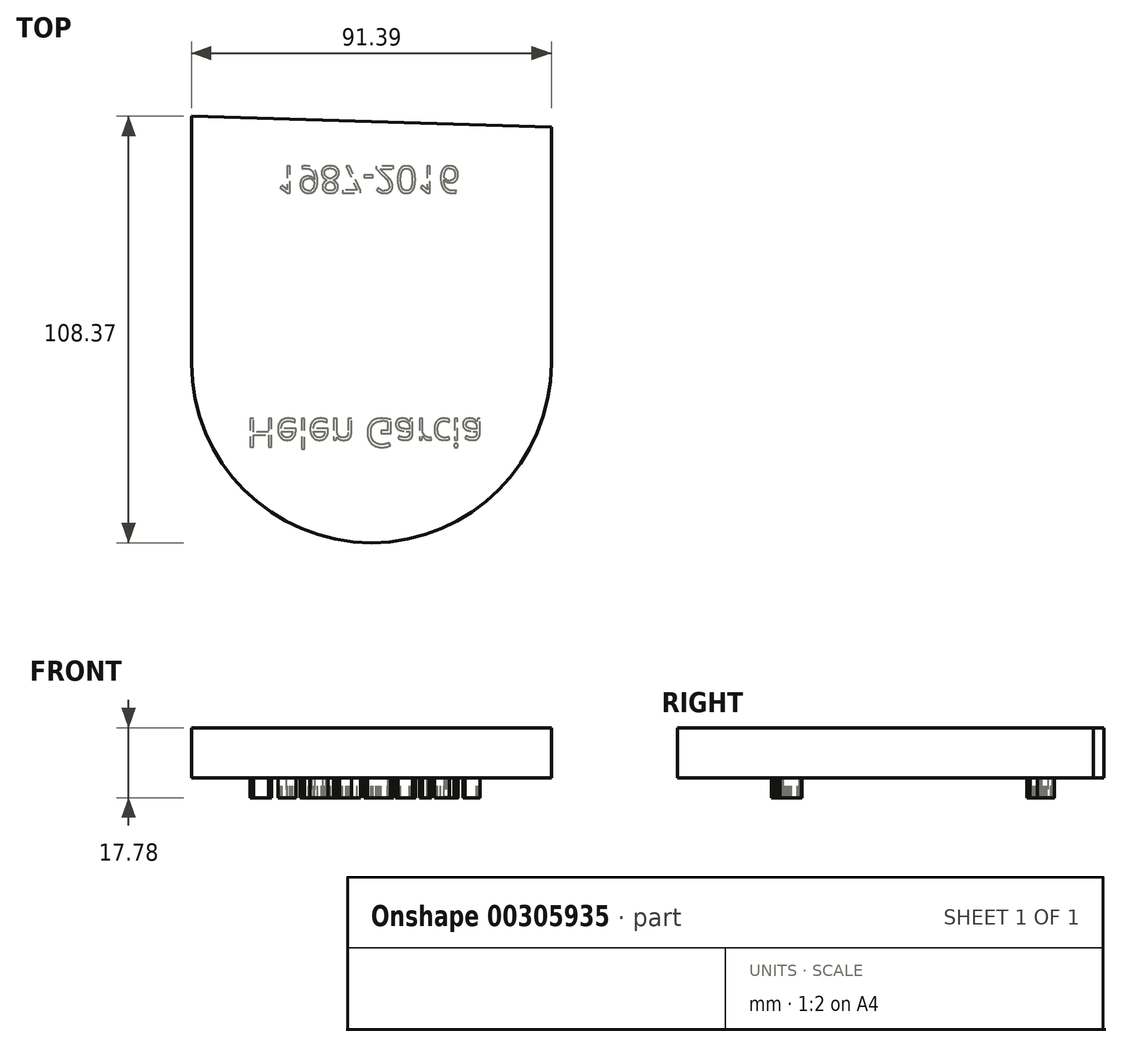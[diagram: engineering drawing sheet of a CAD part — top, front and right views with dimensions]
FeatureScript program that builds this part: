
annotation { "Feature Type Name" : "Feature", "Feature Type Description" : "" }
export const myFeature = defineFeature(function(context is Context, id is Id, definition is map)
    precondition{}
    {
        {
            var Q0;
            Q0=qCreatedBy(makeId("Top.planeOp"),FACE);
            var sketch = newSketch(context, id + "F0", { "sketchPlane" : qUnion([Q0])});
            skLineSegment(sketch, "E0", {"start": v(-124.46, -28.3) * mm, "end": v(-124.46, 34.37) * mm});
            skLineSegment(sketch, "E1", {"start": v(-33.07, -28.3) * mm, "end": v(-33.07, 31.66) * mm});
            skLineSegment(sketch, "E2", {"start": v(-124.46, 34.37) * mm, "end": v(-33.07, 31.66) * mm});
            skArc(sketch, "E3", {"start": v(-124.46, -28.3) * mm, "mid": v(-78.77, -74) * mm, "end": v(-33.07, -28.3) * mm});
            skSolve(sketch);
        }
        {
            var Q0;
            Q0 = qSketchRegion(id + "F0", true);
            extrude(context, id + "F1", {"entities" : qUnion([Q0]), "depth" : 12.7 * mm});
        }
        {
            var Q0;
            Q0=makeQuery(id+"F1.opExtrude","CAP_FACE",FACE,{"disambiguationData":[OSD([sQuery(id+"F0.wireOp",EDGE,"E0"),sQuery(id+"F0.wireOp",EDGE,"E1"),sQuery(id+"F0.wireOp",EDGE,"E2"),sQuery(id+"F0.wireOp",EDGE,"E3")])],"isStart":true});
            var sketch = newSketch(context, id + "F2", { "sketchPlane" : qUnion([Q0])});
            skText(sketch, "E4", { "text": "Helen Garcia ", "fontName": "OpenSans-Regular.ttf"});
            skText(sketch, "E5", { "text": "1987-2016", "fontName": "OpenSans-Regular.ttf"});
            const initialGuessF2  = {"E4": [-0.11054, 0.04247, 1, 0, 0.00726], "E5": [-0.1028, -0.02167, 1, 0, 0.00684]};
            skSetInitialGuess(sketch, initialGuessF2);
            skSolve(sketch);
        }
        {
            var Q0;
            Q0 = qSketchRegion(id + "F2", true);
            extrude(context, id + "F3", {"entities" : qUnion([Q0]), "operationType" : NewBodyOperationType.ADD, "depth" : 5.08 * mm});
        }
    });
